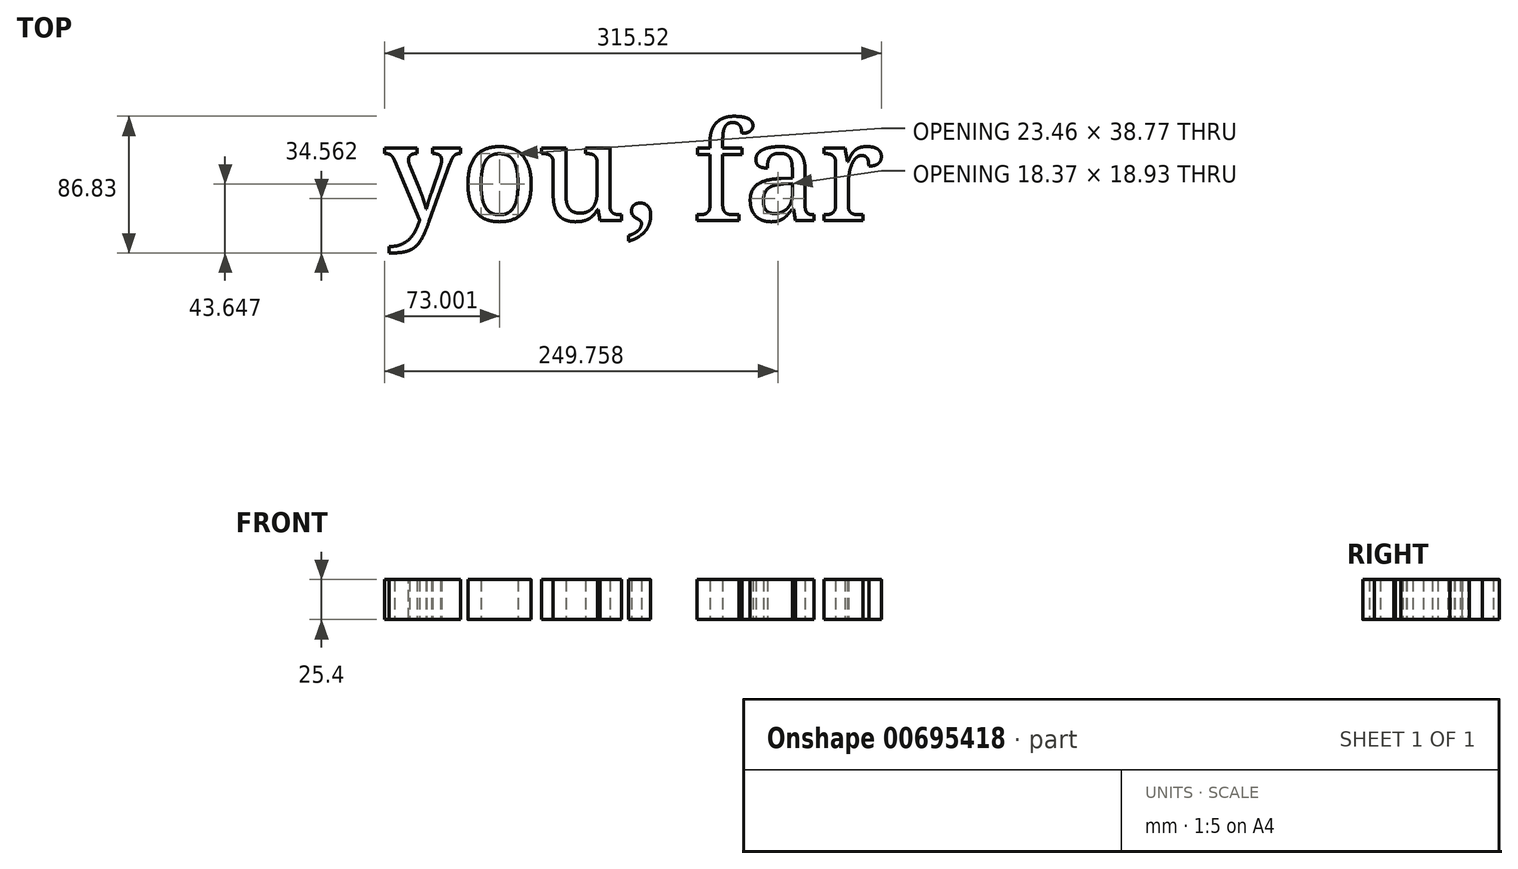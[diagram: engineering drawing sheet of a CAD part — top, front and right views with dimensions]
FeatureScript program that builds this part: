
annotation { "Feature Type Name" : "Feature", "Feature Type Description" : "" }
export const myFeature = defineFeature(function(context is Context, id is Id, definition is map)
    precondition{}
    {
        {
            var Q0;
            Q0=qCreatedBy(makeId("Top.planeOp"),FACE);
            var sketch = newSketch(context, id + "F0", { "sketchPlane" : qUnion([Q0])});
            skText(sketch, "E0", { "text": "you, far", "fontName": "NotoSerif-Regular.ttf"});
            const initialGuessF0  = {"E0": [-0.16088, -0.01166, 1, 0, 0.06188]};
            skSetInitialGuess(sketch, initialGuessF0);
            skSolve(sketch);
        }
        {
            var Q0;
            Q0 = qSketchRegion(id + "F0", true);
            extrude(context, id + "F1", {"entities" : qUnion([Q0]), "depth" : 25.4 * mm, "offsetDistance" : 25.4 * mm});
        }
    });
